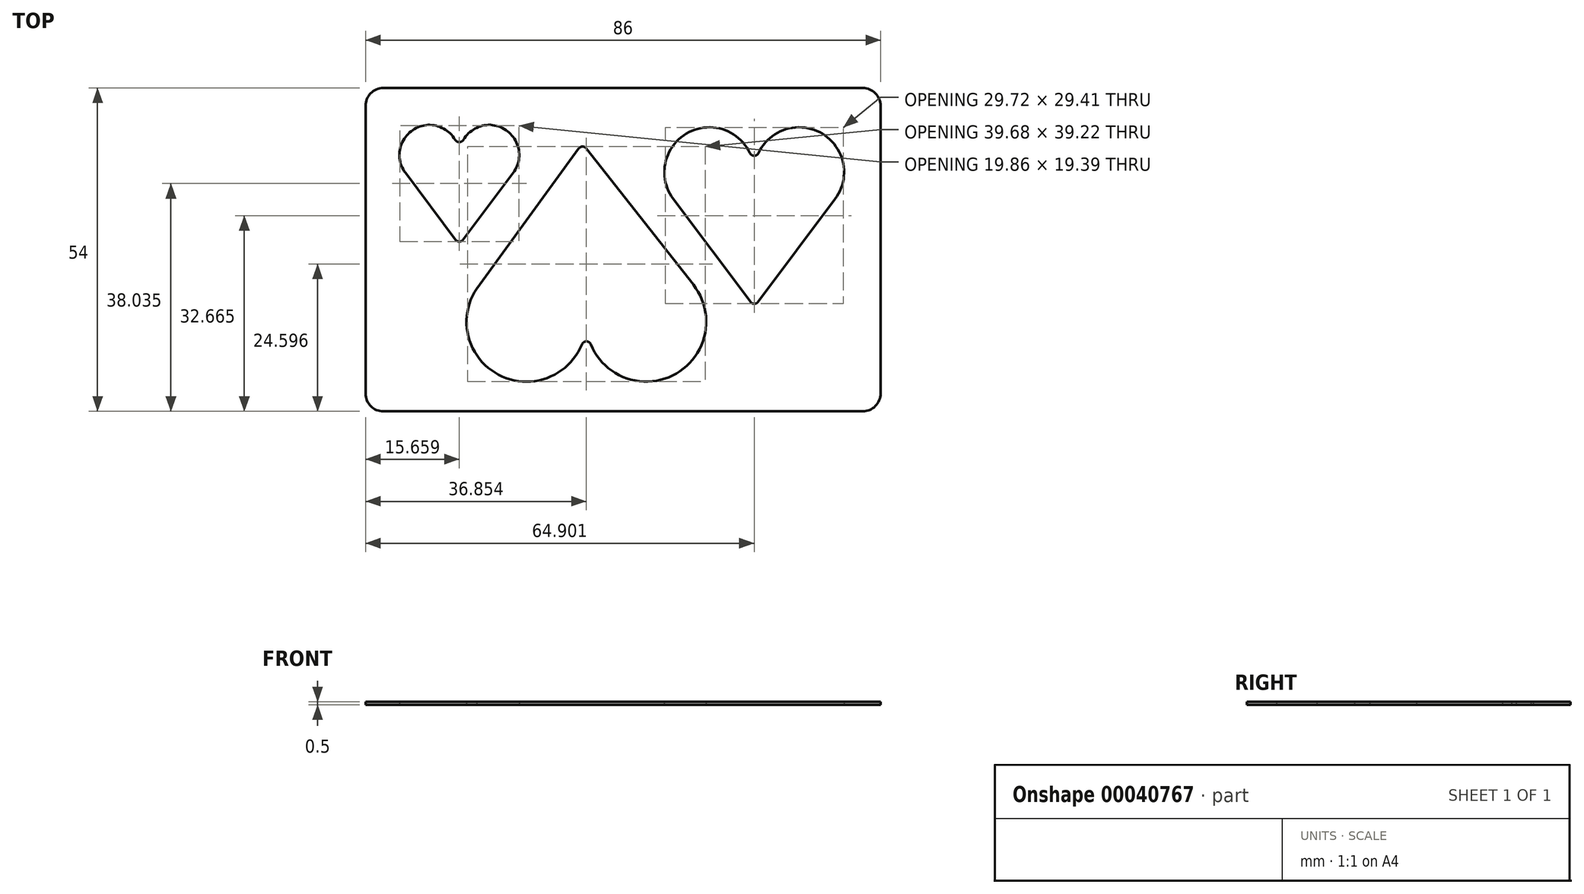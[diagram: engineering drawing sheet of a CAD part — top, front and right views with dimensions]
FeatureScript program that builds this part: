
annotation { "Feature Type Name" : "Feature", "Feature Type Description" : "" }
export const myFeature = defineFeature(function(context is Context, id is Id, definition is map)
    precondition{}
    {
        {
            var Q0;
            Q0=qCreatedBy(makeId("Top.planeOp"),FACE);
            var sketch = newSketch(context, id + "F0", { "sketchPlane" : qUnion([Q0])});
            skLineSegment(sketch, "E0.bottom", {"start": v(-40, -26.1) * mm, "end": v(40, -26.1) * mm});
            skLineSegment(sketch, "E0.top", {"start": v(-40, 27.9) * mm, "end": v(40, 27.9) * mm});
            skLineSegment(sketch, "E0.left", {"start": v(-43, -23.1) * mm, "end": v(-43, 24.9) * mm});
            skLineSegment(sketch, "E0.right", {"start": v(43, -23.1) * mm, "end": v(43, 24.9) * mm});
            skPoint(sketch, "E1.visualSharp", {"position": v(-43, 27.9) * mm});
            skArc(sketch, "E1.filletArc", {"start": v(-40, 27.9) * mm, "mid": v(-42.12, 27.02) * mm, "end": v(-43, 24.9) * mm});
            skPoint(sketch, "E2.visualSharp", {"position": v(-43, -26.1) * mm});
            skArc(sketch, "E2.filletArc", {"start": v(-43, -23.1) * mm, "mid": v(-42.12, -25.22) * mm, "end": v(-40, -26.1) * mm});
            skPoint(sketch, "E3.visualSharp", {"position": v(43, 27.9) * mm});
            skArc(sketch, "E3.filletArc", {"start": v(43, 24.9) * mm, "mid": v(42.12, 27.02) * mm, "end": v(40, 27.9) * mm});
            skPoint(sketch, "E4.visualSharp", {"position": v(43, -26.1) * mm});
            skArc(sketch, "E4.filletArc", {"start": v(40, -26.1) * mm, "mid": v(42.12, -25.22) * mm, "end": v(43, -23.1) * mm});
            skLineSegment(sketch, "E5", {"start": v(-36.34, 13.7) * mm, "end": v(-27.98, 2.56) * mm});
            skLineSegment(sketch, "E6", {"start": v(-26.7, 2.56) * mm, "end": v(-18.34, 13.7) * mm});
            skLineSegment(sketch, "E7", {"start": v(-32.34, 16.7) * mm, "end": v(-27.34, 16.7) * mm, "construction": true});
            skLineSegment(sketch, "E8", {"start": v(8.4, 9.33) * mm, "end": v(21.26, -7.82) * mm});
            skLineSegment(sketch, "E9", {"start": v(22.54, -7.82) * mm, "end": v(35.4, 9.33) * mm});
            skLineSegment(sketch, "E10", {"start": v(14.4, 13.83) * mm, "end": v(21.9, 13.83) * mm, "construction": true});
            skLineSegment(sketch, "E11", {"start": v(-24.46, -5.6) * mm, "end": v(-7.4, 17.78) * mm});
            skLineSegment(sketch, "E12", {"start": v(-6.13, 17.8) * mm, "end": v(11.74, -4.96) * mm});
            skLineSegment(sketch, "E13", {"start": v(-16.13, -11.14) * mm, "end": v(-6.13, -11.14) * mm, "construction": true});
            skPoint(sketch, "E14.visualSharp", {"position": v(-6.79, 18.63) * mm});
            skArc(sketch, "E15.filletArc", {"start": v(-6.13, 17.8) * mm, "mid": v(-6.78, 18.1) * mm, "end": v(-7.4, 17.78) * mm});
            skPoint(sketch, "E16.visualSharp", {"position": v(-27.34, 1.7) * mm});
            skArc(sketch, "E16.filletArc", {"start": v(-27.98, 2.56) * mm, "mid": v(-27.34, 2.24) * mm, "end": v(-26.7, 2.56) * mm});
            skLineSegment(sketch, "E17", {"start": v(-27.34, 16.7) * mm, "end": v(-22.34, 16.7) * mm, "construction": true});
            skArc(sketch, "E18", {"start": v(-18.34, 13.7) * mm, "mid": v(-19.57, 20.87) * mm, "end": v(-26.65, 19.24) * mm});
            skArc(sketch, "E19", {"start": v(-28.03, 19.24) * mm, "mid": v(-35.11, 20.87) * mm, "end": v(-36.34, 13.7) * mm});
            skPoint(sketch, "E20.visualSharp", {"position": v(-27.34, 16.7) * mm});
            skArc(sketch, "E20.filletArc", {"start": v(-28.03, 19.24) * mm, "mid": v(-27.34, 18.85) * mm, "end": v(-26.65, 19.24) * mm});
            skLineSegment(sketch, "E21", {"start": v(21.9, 13.83) * mm, "end": v(29.4, 13.83) * mm, "construction": true});
            skArc(sketch, "E22", {"start": v(21.18, 17.04) * mm, "mid": v(10.53, 20.25) * mm, "end": v(8.4, 9.33) * mm});
            skArc(sketch, "E23", {"start": v(35.4, 9.33) * mm, "mid": v(33.28, 20.25) * mm, "end": v(22.62, 17.04) * mm});
            skPoint(sketch, "E24.visualSharp", {"position": v(21.9, 13.83) * mm});
            skArc(sketch, "E24.filletArc", {"start": v(21.18, 17.04) * mm, "mid": v(21.9, 16.58) * mm, "end": v(22.62, 17.04) * mm});
            skPoint(sketch, "E25.visualSharp", {"position": v(21.9, -8.67) * mm});
            skArc(sketch, "E25.filletArc", {"start": v(21.26, -7.82) * mm, "mid": v(21.9, -8.14) * mm, "end": v(22.54, -7.82) * mm});
            skLineSegment(sketch, "E26", {"start": v(-6.13, -11.14) * mm, "end": v(3.87, -11.14) * mm, "construction": true});
            skArc(sketch, "E27", {"start": v(-24.46, -5.6) * mm, "mid": v(-20.8, -19.98) * mm, "end": v(-6.87, -14.92) * mm});
            skArc(sketch, "E28", {"start": v(-5.39, -14.92) * mm, "mid": v(8.9, -19.79) * mm, "end": v(11.74, -4.96) * mm});
            skPoint(sketch, "E29.visualSharp", {"position": v(-6.13, -11.14) * mm});
            skArc(sketch, "E29.filletArc", {"start": v(-5.39, -14.92) * mm, "mid": v(-6.13, -14.42) * mm, "end": v(-6.87, -14.92) * mm});
            skSolve(sketch);
        }
        {
            var Q0;
            Q0=makeQuery(id+"F0.imprint","IMPRINT",FACE,{"disambiguationData":[TD([[makeQuery(id+"F0.imprint","IMPRINT",EDGE,{"derivedFrom":sQuery(id+"F0.wireOp",EDGE,"E0.bottom")}),1.0]])]});
            extrude(context, id + "F1", {"entities" : qUnion([Q0]), "depth" : 0.5 * mm});
        }
    });
